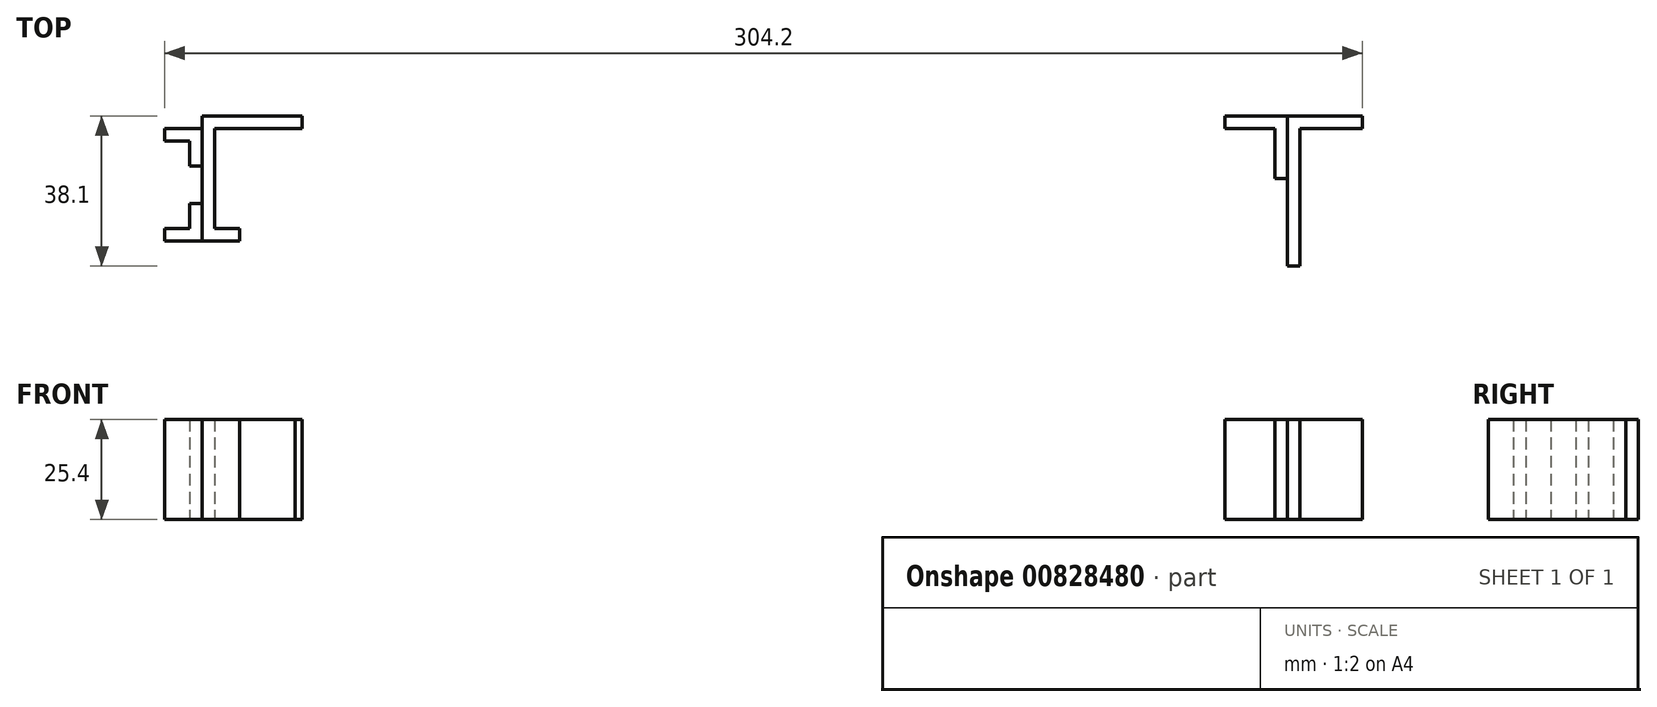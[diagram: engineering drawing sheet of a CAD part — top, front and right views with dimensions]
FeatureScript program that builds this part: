
annotation { "Feature Type Name" : "Feature", "Feature Type Description" : "" }
export const myFeature = defineFeature(function(context is Context, id is Id, definition is map)
    precondition{}
    {
        {
            var Q0;
            Q0=qCreatedBy(makeId("Top.planeOp"),FACE);
            var sketch = newSketch(context, id + "F0", { "sketchPlane" : qUnion([Q0])});
            skLineSegment(sketch, "E0.bottom", {"start": v(0, 0) * mm, "end": v(254, 0) * mm});
            skLineSegment(sketch, "E0.top", {"start": v(0, 19.05) * mm, "end": v(254, 19.05) * mm});
            skLineSegment(sketch, "E0.left", {"start": v(0, 0) * mm, "end": v(0, 19.05) * mm});
            skLineSegment(sketch, "E0.right", {"start": v(254, 0) * mm, "end": v(254, 19.05) * mm});
            skLineSegment(sketch, "E1.bottom", {"start": v(2.54, 19.05) * mm, "end": v(12.06, 19.05) * mm});
            skLineSegment(sketch, "E1.top", {"start": v(2.54, 21.59) * mm, "end": v(12.06, 21.59) * mm});
            skLineSegment(sketch, "E1.left", {"start": v(2.54, 19.05) * mm, "end": v(2.54, 21.59) * mm});
            skLineSegment(sketch, "E1.right", {"start": v(12.06, 19.05) * mm, "end": v(12.06, 21.59) * mm});
            skLineSegment(sketch, "E2.bottom", {"start": v(12.06, 21.59) * mm, "end": v(-10.16, 21.59) * mm});
            skLineSegment(sketch, "E2.top", {"start": v(12.06, 24.77) * mm, "end": v(-13.33, 24.77) * mm});
            skLineSegment(sketch, "E2.left", {"start": v(12.06, 21.59) * mm, "end": v(12.06, 24.77) * mm});
            skLineSegment(sketch, "E3.left", {"start": v(-13.34, 21.59) * mm, "end": v(-13.34, -3.8) * mm});
            skLineSegment(sketch, "E3.right", {"start": v(-10.16, 21.59) * mm, "end": v(-10.16, -3.8) * mm});
            skLineSegment(sketch, "E4.bottom", {"start": v(-3.81, -3.8) * mm, "end": v(-10.16, -3.8) * mm});
            skLineSegment(sketch, "E4.top", {"start": v(-3.81, -6.98) * mm, "end": v(-22.86, -6.99) * mm});
            skLineSegment(sketch, "E4.left", {"start": v(-3.81, -3.8) * mm, "end": v(-3.81, -6.98) * mm});
            skLineSegment(sketch, "E4.right", {"start": v(-22.86, -3.81) * mm, "end": v(-22.86, -6.99) * mm});
            skLineSegment(sketch, "E5", {"start": v(3.4, 21.52) * mm, "end": v(4.18, 20.34) * mm});
            skLineSegment(sketch, "E6", {"start": v(4.18, 20.34) * mm, "end": v(5.18, 21) * mm});
            skLineSegment(sketch, "E7", {"start": v(5.18, 21) * mm, "end": v(5.62, 20.34) * mm});
            skLineSegment(sketch, "E8", {"start": v(5.62, 20.34) * mm, "end": v(7.01, 21.27) * mm});
            skLineSegment(sketch, "E9", {"start": v(7.01, 21.27) * mm, "end": v(7.63, 20.34) * mm});
            skLineSegment(sketch, "E10", {"start": v(7.63, 20.34) * mm, "end": v(9, 21.26) * mm});
            skLineSegment(sketch, "E11", {"start": v(9, 21.26) * mm, "end": v(9.62, 19.05) * mm});
            skLineSegment(sketch, "E12", {"start": v(9.62, 19.05) * mm, "end": v(10.2, 21.72) * mm});
            skLineSegment(sketch, "E13", {"start": v(10.2, 21.72) * mm, "end": v(10.93, 20.34) * mm});
            skLineSegment(sketch, "E14.bottom", {"start": v(246.41, 19.05) * mm, "end": v(252.4, 19.05) * mm});
            skLineSegment(sketch, "E14.top", {"start": v(246.41, 21.6) * mm, "end": v(252.4, 21.6) * mm});
            skLineSegment(sketch, "E14.left", {"start": v(246.41, 19.05) * mm, "end": v(246.41, 21.6) * mm});
            skLineSegment(sketch, "E14.right", {"start": v(252.4, 19.05) * mm, "end": v(252.4, 21.6) * mm});
            skLineSegment(sketch, "E15.bottom", {"start": v(246.41, 21.6) * mm, "end": v(259.11, 21.6) * mm});
            skLineSegment(sketch, "E15.top", {"start": v(246.41, 24.77) * mm, "end": v(281.34, 24.77) * mm});
            skLineSegment(sketch, "E15.left", {"start": v(246.41, 21.6) * mm, "end": v(246.41, 24.77) * mm});
            skLineSegment(sketch, "E15.right", {"start": v(281.34, 21.6) * mm, "end": v(281.34, 24.77) * mm});
            skLineSegment(sketch, "E16.bottom", {"start": v(262.29, -13.33) * mm, "end": v(265.46, -13.34) * mm});
            skLineSegment(sketch, "E16.left", {"start": v(265.46, -13.34) * mm, "end": v(265.46, 21.6) * mm});
            skLineSegment(sketch, "E16.right", {"start": v(262.29, -13.34) * mm, "end": v(262.29, 21.6) * mm});
            skLineSegment(sketch, "E17.bottom", {"start": v(-22.86, 18.41) * mm, "end": v(-16.51, 18.41) * mm});
            skLineSegment(sketch, "E17.top", {"start": v(-22.86, 21.59) * mm, "end": v(-13.33, 21.59) * mm});
            skLineSegment(sketch, "E17.left", {"start": v(-22.86, 18.41) * mm, "end": v(-22.86, 21.59) * mm});
            skLineSegment(sketch, "E17.right", {"start": v(-13.33, 18.41) * mm, "end": v(-13.33, 21.59) * mm});
            skLineSegment(sketch, "E18", {"start": v(-13.33, 21.59) * mm, "end": v(-13.33, 24.77) * mm});
            skLineSegment(sketch, "E19", {"start": v(-13.34, -3.8) * mm, "end": v(-13.34, -6.98) * mm});
            skLineSegment(sketch, "E20", {"start": v(-16.51, -3.8) * mm, "end": v(-16.51, 2.54) * mm});
            skLineSegment(sketch, "E21", {"start": v(-16.51, 2.54) * mm, "end": v(-13.34, 2.54) * mm});
            skLineSegment(sketch, "E22.trimOffspring", {"start": v(-13.34, 21.59) * mm, "end": v(-22.86, 21.59) * mm});
            skLineSegment(sketch, "E23.trimOffspring", {"start": v(-16.51, -3.8) * mm, "end": v(-22.86, -3.81) * mm});
            skLineSegment(sketch, "E24", {"start": v(-16.51, 18.41) * mm, "end": v(-16.51, 12.07) * mm});
            skLineSegment(sketch, "E25", {"start": v(-16.51, 12.07) * mm, "end": v(-13.34, 12.07) * mm});
            skLineSegment(sketch, "E26", {"start": v(262.29, 21.6) * mm, "end": v(262.29, 24.77) * mm});
            skLineSegment(sketch, "E27", {"start": v(259.11, 21.6) * mm, "end": v(259.11, 8.89) * mm});
            skLineSegment(sketch, "E28", {"start": v(259.11, 8.89) * mm, "end": v(262.29, 8.89) * mm});
            skLineSegment(sketch, "E29.trimOffspring", {"start": v(265.46, 21.6) * mm, "end": v(281.34, 21.6) * mm});
            skPoint(sketch, "E30.end.orphan", {"position": v(263.88, -13.33) * mm});
            skPoint(sketch, "E30.start.orphan", {"position": v(263.88, 21.6) * mm});
            skLineSegment(sketch, "E31", {"start": v(319.1, 21.6) * mm, "end": v(347.4, 21.6) * mm});
            skLineSegment(sketch, "E32", {"start": v(347.4, 21.6) * mm, "end": v(347.4, -13.33) * mm});
            skLineSegment(sketch, "E33", {"start": v(347.4, -13.33) * mm, "end": v(349.94, -13.33) * mm});
            skLineSegment(sketch, "E34", {"start": v(349.94, -13.33) * mm, "end": v(349.94, 23.23) * mm});
            skLineSegment(sketch, "E35", {"start": v(349.94, 23.23) * mm, "end": v(319.1, 23.23) * mm});
            skLineSegment(sketch, "E36", {"start": v(319.1, 23.23) * mm, "end": v(319.1, 21.6) * mm});
            skLineSegment(sketch, "E37", {"start": v(349.94, 23.23) * mm, "end": v(378.35, 23.23) * mm});
            skLineSegment(sketch, "E38", {"start": v(378.35, 23.23) * mm, "end": v(378.35, 21.6) * mm});
            skLineSegment(sketch, "E39", {"start": v(378.35, 21.6) * mm, "end": v(352.14, 21.6) * mm});
            skLineSegment(sketch, "E40", {"start": v(352.14, 21.6) * mm, "end": v(352.14, -13.33) * mm});
            skLineSegment(sketch, "E41", {"start": v(352.14, -13.33) * mm, "end": v(349.94, -13.33) * mm});
            skLineSegment(sketch, "E42", {"start": v(319.1, 23.23) * mm, "end": v(319.1, 25.28) * mm});
            skLineSegment(sketch, "E43", {"start": v(319.1, 25.28) * mm, "end": v(378.35, 25.28) * mm});
            skLineSegment(sketch, "E44", {"start": v(378.35, 25.28) * mm, "end": v(378.35, 23.23) * mm});
            skLineSegment(sketch, "E45.bottom", {"start": v(-22.86, 56.51) * mm, "end": v(-29.21, 56.51) * mm});
            skLineSegment(sketch, "E45.top", {"start": v(-22.86, -19.69) * mm, "end": v(-29.21, -19.69) * mm});
            skLineSegment(sketch, "E45.left", {"start": v(-22.86, 56.51) * mm, "end": v(-22.86, -19.69) * mm});
            skLineSegment(sketch, "E45.right", {"start": v(-29.21, 56.51) * mm, "end": v(-29.21, -19.69) * mm});
            skSolve(sketch);
        }
        {
            var Q0;
            Q0=makeQuery(id+"F0.imprint","IMPRINT",FACE,{"disambiguationData":[TD([[makeQuery(id+"F0.imprint","IMPRINT",EDGE,{"derivedFrom":sQuery(id+"F0.wireOp",EDGE,"E2.top")}),1.0]])]});
            extrude(context, id + "F1", {"entities" : qUnion([Q0]), "depth" : 25.4 * mm, "offsetDistance" : 25.4 * mm});
        }
        {
            var Q0;
            {var subQ0=sQuery(id+"F0.wireOp",EDGE,"E17.bottom");Q0=makeQuery(id+"F0.imprint","IMPRINT",FACE,{"disambiguationData":[TD([[makeQuery(id+"F0.imprint","IMPRINT",EDGE,{"derivedFrom":subQ0}),1.0]])]});}
            var Q1;
            {var subQ3=sQuery(id+"F0.wireOp",EDGE,"E19");Q1=makeQuery(id+"F0.imprint","IMPRINT",FACE,{"disambiguationData":[TD([[makeQuery(id+"F0.imprint","IMPRINT",EDGE,{"derivedFrom":subQ3}),-1.0]])]});}
            extrude(context, id + "F2", {"entities" : qUnion([Q0, Q1]), "depth" : 25.4 * mm, "offsetDistance" : 25.4 * mm});
        }
        {
            var Q0;
            {var subQ1=sQuery(id+"F0.wireOp",EDGE,"E15.right");Q0=makeQuery(id+"F0.imprint","IMPRINT",FACE,{"disambiguationData":[TD([[makeQuery(id+"F0.imprint","IMPRINT",EDGE,{"derivedFrom":subQ1}),1.0]])]});}
            extrude(context, id + "F3", {"entities" : qUnion([Q0]), "depth" : 25.4 * mm, "offsetDistance" : 25.4 * mm});
        }
        {
            var Q0;
            {var subQ0=sQuery(id+"F0.wireOp",EDGE,"E15.left");Q0=makeQuery(id+"F0.imprint","IMPRINT",FACE,{"disambiguationData":[TD([[makeQuery(id+"F0.imprint","IMPRINT",EDGE,{"derivedFrom":subQ0}),-1.0]])]});}
            extrude(context, id + "F4", {"entities" : qUnion([Q0]), "depth" : 25.4 * mm, "offsetDistance" : 25.4 * mm});
        }
    });
